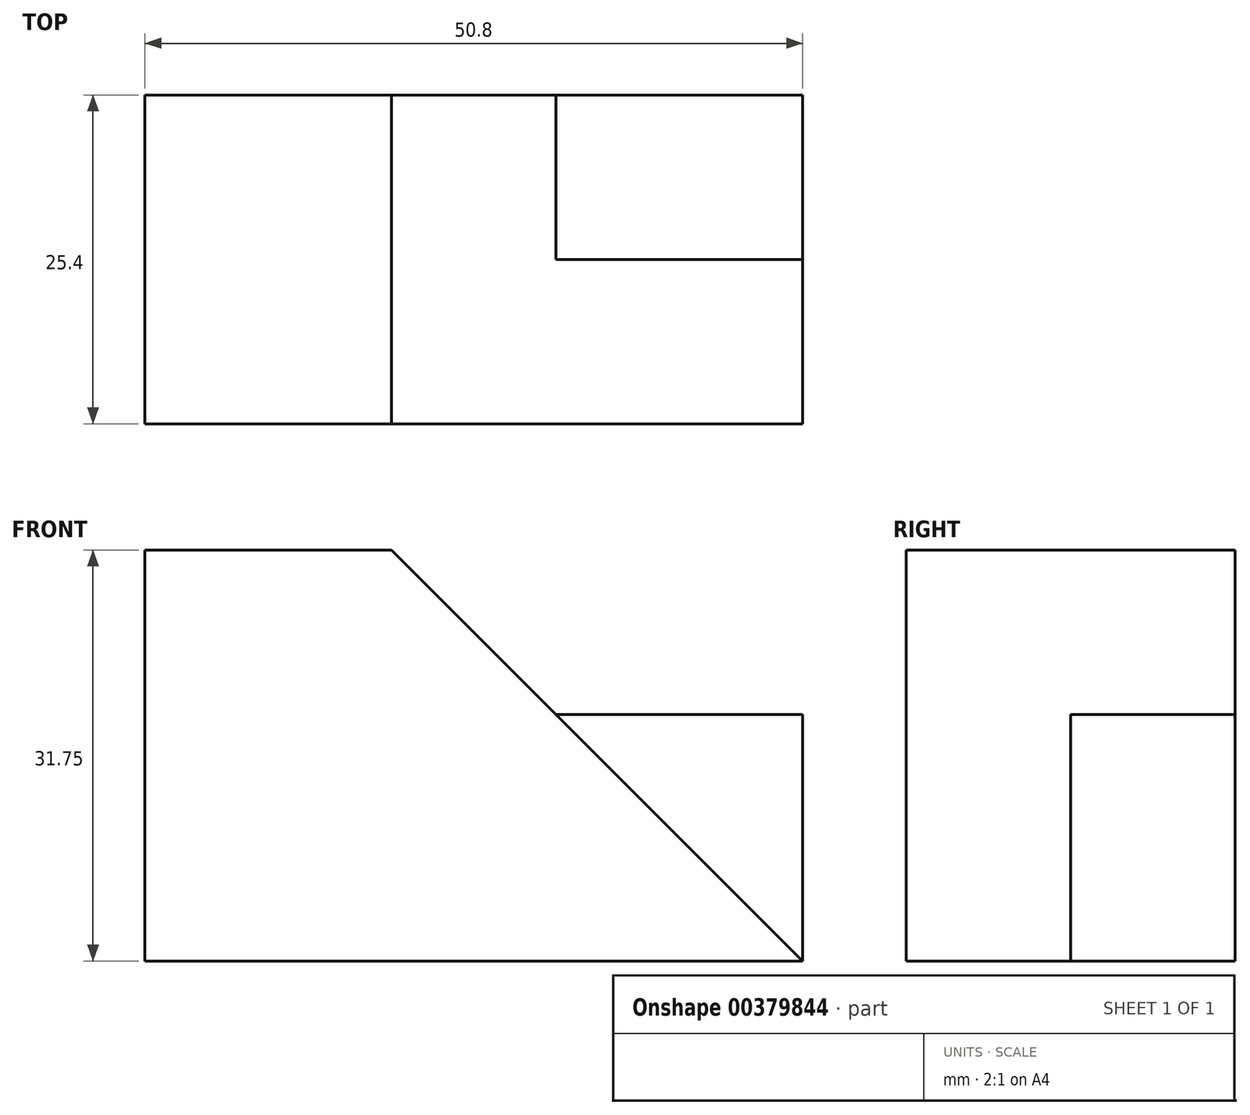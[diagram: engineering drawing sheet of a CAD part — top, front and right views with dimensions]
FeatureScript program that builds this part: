
annotation { "Feature Type Name" : "Feature", "Feature Type Description" : "" }
export const myFeature = defineFeature(function(context is Context, id is Id, definition is map)
    precondition{}
    {
        {
            var Q0;
            Q0=qCreatedBy(makeId("Front.planeOp"),FACE);
            var sketch = newSketch(context, id + "F0", { "sketchPlane" : qUnion([Q0])});
            skLineSegment(sketch, "E0", {"start": v(0, 31.75) * mm, "end": v(50.8, 31.75) * mm});
            skLineSegment(sketch, "E1", {"start": v(50.8, 31.75) * mm, "end": v(50.8, 0) * mm});
            skLineSegment(sketch, "E2", {"start": v(0, 31.75) * mm, "end": v(0, 0) * mm});
            skLineSegment(sketch, "E3", {"start": v(0, 0) * mm, "end": v(50.8, 0) * mm});
            skSolve(sketch);
        }
        {
            var Q0;
            Q0=makeQuery(id+"F0.imprint","IMPRINT",FACE,{"disambiguationData":[TD([[makeQuery(id+"F0.imprint","IMPRINT",EDGE,{"derivedFrom":sQuery(id+"F0.wireOp",EDGE,"E0")}),-1.0]])]});
            extrude(context, id + "F1", {"entities" : qUnion([Q0]), "depth" : 25.4 * mm});
        }
        {
            var Q0;
            Q0=qCreatedBy(makeId("Right.planeOp"),FACE);
            var sketch = newSketch(context, id + "F2", { "sketchPlane" : qUnion([Q0])});
            skLineSegment(sketch, "E4", {"start": v(-15.33, 32.34) * mm, "end": v(-15.33, 0) * mm});
            skSolve(sketch);
        }
        {
            var Q0;
            Q0=makeQuery(id+"F1.opExtrude","CAP_FACE",FACE,{"disambiguationData":[OSD([sQuery(id+"F0.wireOp",EDGE,"E0"),sQuery(id+"F0.wireOp",EDGE,"E1"),sQuery(id+"F0.wireOp",EDGE,"E2"),sQuery(id+"F0.wireOp",EDGE,"E3")])],"isStart":false});
            var sketch = newSketch(context, id + "F3", { "sketchPlane" : qUnion([Q0])});
            skLineSegment(sketch, "E5", {"start": v(50.8, 0) * mm, "end": v(19.05, 31.75) * mm});
            skSolve(sketch);
        }
        {
            var Q0;
            {var subQ0=sQuery(id+"F3.wireOp",EDGE,"E5");Q0=makeQuery(id+"F3.imprint","IMPRINT",FACE,{"disambiguationData":[TD([[makeQuery(id+"F3.imprint","IMPRINT",EDGE,{"derivedFrom":subQ0}),-1.0]])]});}
            extrude(context, id + "F4", {"entities" : qUnion([Q0]), "operationType" : NewBodyOperationType.REMOVE, "oppositeDirection" : true, "depth" : 12.7 * mm});
        }
        {
            var Q0;
            Q0=makeQuery(id+"F4.boolean.opBoolean","COPY",FACE,{"derivedFrom":makeQuery(id+"F4.opExtrude","CAP_FACE",FACE,{"disambiguationData":[OSD([sQuery(id+"F0.wireOp",EDGE,"E0"),sQuery(id+"F0.wireOp",EDGE,"E1"),sQuery(id+"F3.wireOp",EDGE,"E5")])],"isStart":false})});
            var sketch = newSketch(context, id + "F5", { "sketchPlane" : qUnion([Q0])});
            skLineSegment(sketch, "E6", {"start": v(31.75, 19.05) * mm, "end": v(50.8, 19.05) * mm});
            skSolve(sketch);
        }
        {
            var Q0;
            {var subQ0=sQuery(id+"F5.wireOp",EDGE,"E6");Q0=makeQuery(id+"F5.imprint","IMPRINT",FACE,{"disambiguationData":[TD([[makeQuery(id+"F5.imprint","IMPRINT",EDGE,{"derivedFrom":subQ0}),1.0]])]});}
            extrude(context, id + "F6", {"entities" : qUnion([Q0]), "operationType" : NewBodyOperationType.REMOVE, "oppositeDirection" : true, "depth" : 19.05 * mm});
        }
    });
